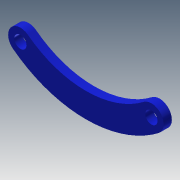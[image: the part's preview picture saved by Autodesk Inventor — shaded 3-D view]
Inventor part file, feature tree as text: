
AUTODESK INVENTOR PART (.ipt)
format: ipt  version: 2013 (Build 170138000, 138)  size: 98,816 bytes
history: native  units: mm
features: extrude x2, sketch x2
ambient origin geometry x8: Origin, YZ Plane, XZ Plane, XY Plane, X Axis, Y Axis, Z Axis, Center Point
bodies: Solid1 (feature_tree)
feature tree (4):
  extrude  "Extrusion1"  Depth=6.0mm
  extrude  "Extrusion2"  Depth=3.0mm
  sketch  "Sketch1"  dims[d2=3.0mm d11=6.0mm]
  sketch  "Sketch2"  dims[d12=2.0mm d13=0.0mm d14=3.0mm d15=3.0mm d16=2.0mm d17=0.0mm]
